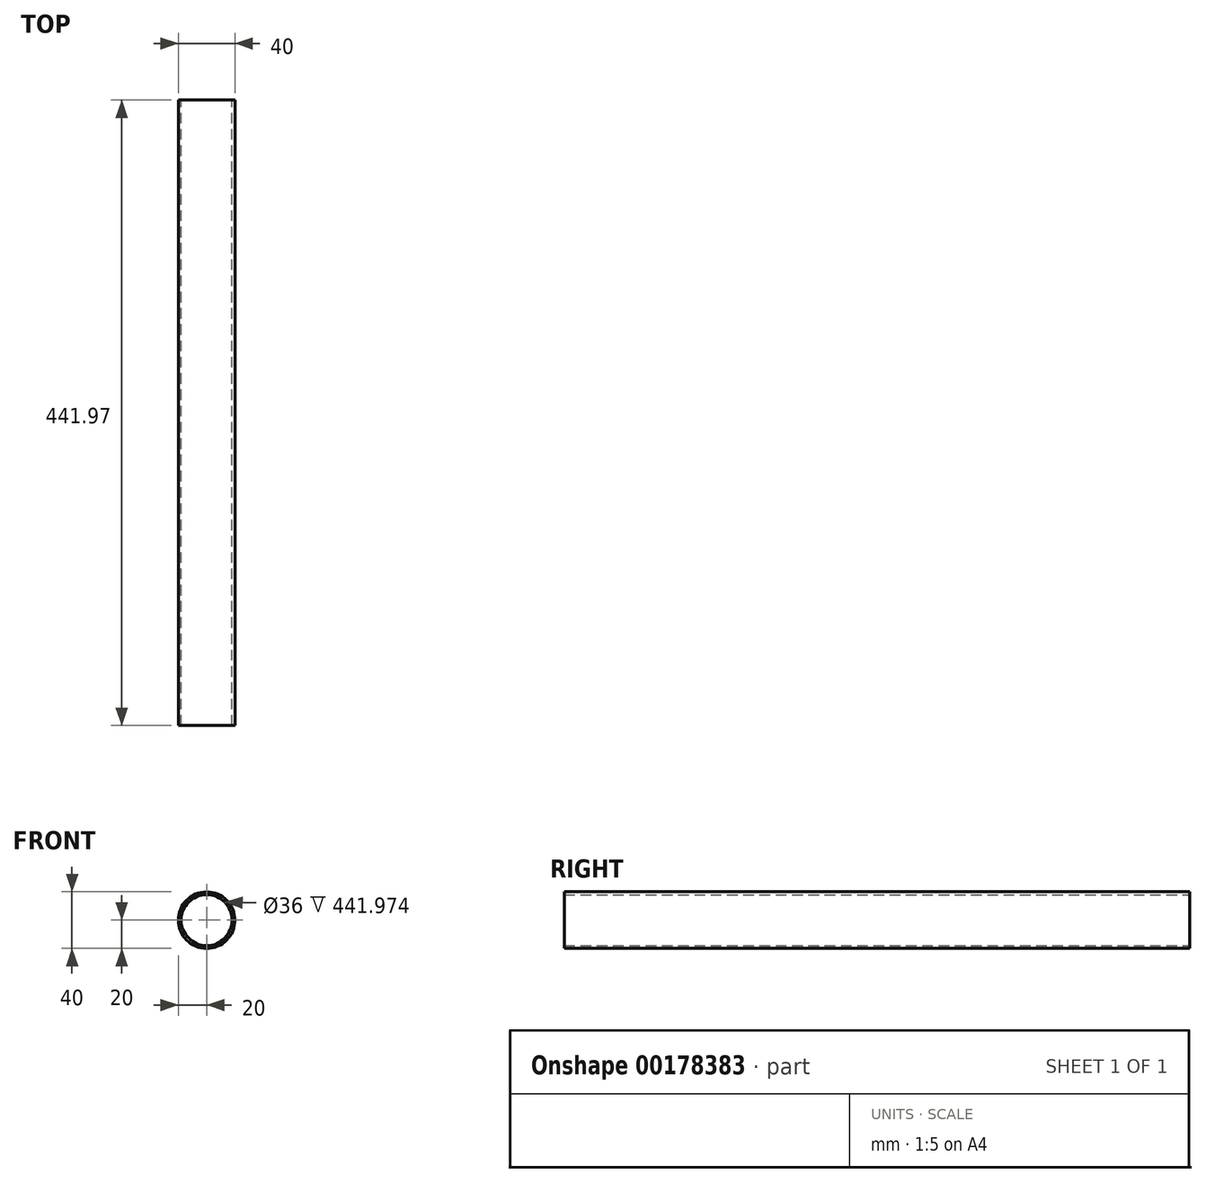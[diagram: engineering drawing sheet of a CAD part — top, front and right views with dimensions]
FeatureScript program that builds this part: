
annotation { "Feature Type Name" : "Feature", "Feature Type Description" : "" }
export const myFeature = defineFeature(function(context is Context, id is Id, definition is map)
    precondition{}
    {
        {
            var Q0;
            Q0=qCreatedBy(makeId("Front.planeOp"),FACE);
            var sketch = newSketch(context, id + "F0", { "sketchPlane" : qUnion([Q0])});
            skCircle(sketch, "E0", {"center": v(0, 0) * mm, "radius": 20 * mm});
            skCircle(sketch, "E1.0", {"center": v(0, 0) * mm, "radius": 18 * mm});
            skSolve(sketch);
        }
        {
            var Q0;
            Q0=makeQuery(id+"F0.imprint","IMPRINT",FACE,{"disambiguationData":[TD([[makeQuery(id+"F0.imprint","IMPRINT",EDGE,{"derivedFrom":sQuery(id+"F0.wireOp",EDGE,"E0")}),1.0]])]});
            extrude(context, id + "F1", {"entities" : qUnion([Q0]), "depth" : 441.97 * mm});
        }
    });
